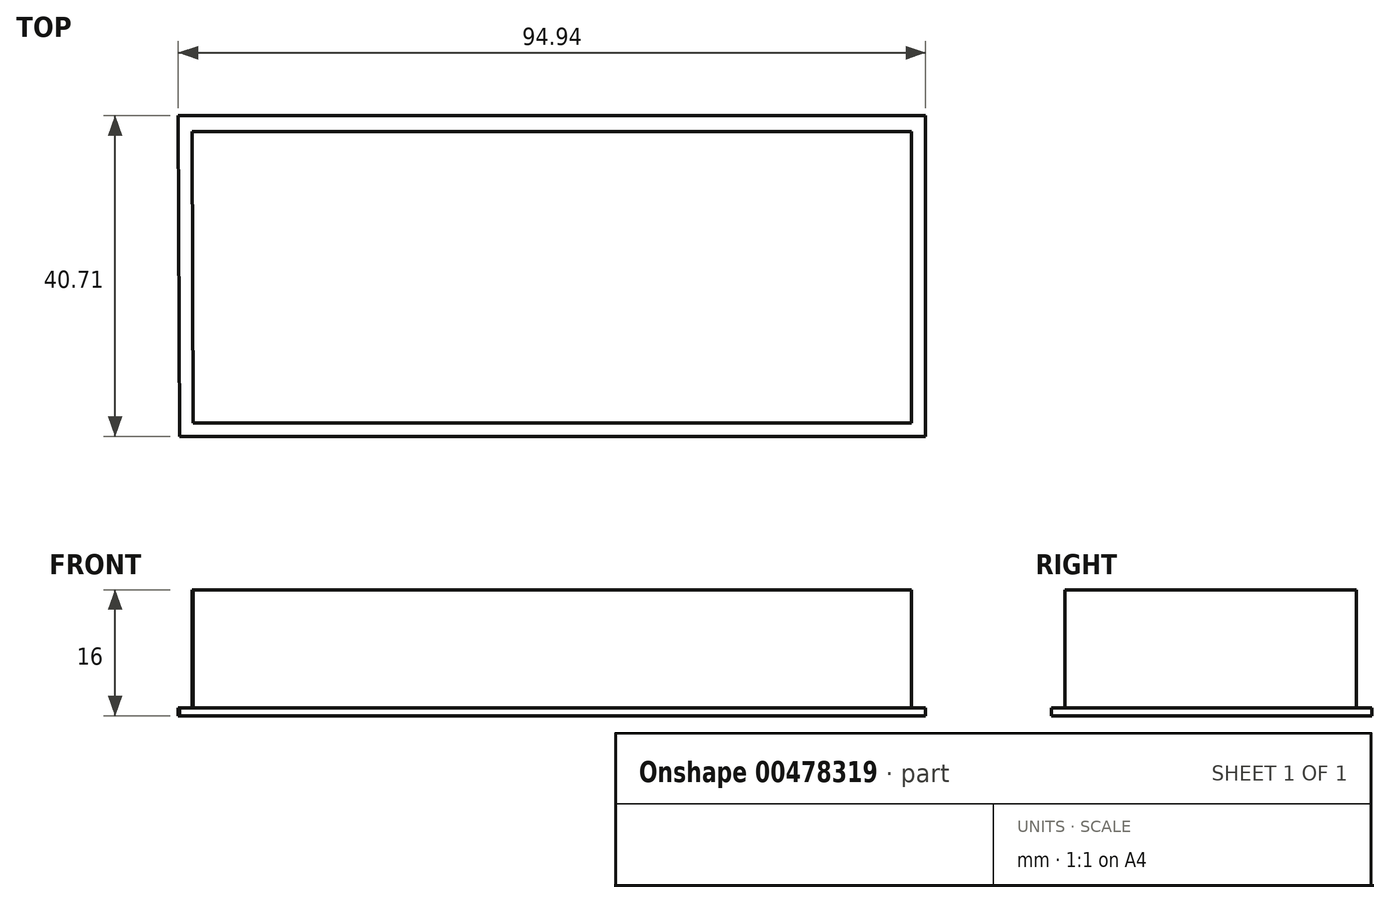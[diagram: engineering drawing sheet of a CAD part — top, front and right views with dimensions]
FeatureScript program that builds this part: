
annotation { "Feature Type Name" : "Feature", "Feature Type Description" : "" }
export const myFeature = defineFeature(function(context is Context, id is Id, definition is map)
    precondition{}
    {
        {
            var Q0;
            Q0=qCreatedBy(makeId("Top.planeOp"),FACE);
            var sketch = newSketch(context, id + "F0", { "sketchPlane" : qUnion([Q0])});
            skLineSegment(sketch, "E0", {"start": v(-48.08, 21.76) * mm, "end": v(46.86, 21.76) * mm});
            skLineSegment(sketch, "E1", {"start": v(46.86, 21.76) * mm, "end": v(46.86, -18.95) * mm});
            skLineSegment(sketch, "E2", {"start": v(46.86, -18.95) * mm, "end": v(-47.92, -18.95) * mm});
            skLineSegment(sketch, "E3", {"start": v(-47.92, -18.95) * mm, "end": v(-48.08, 21.76) * mm});
            skLineSegment(sketch, "E4", {"start": v(-46.16, -17.24) * mm, "end": v(-46.3, 19.76) * mm});
            skLineSegment(sketch, "E5", {"start": v(-46.3, 19.76) * mm, "end": v(45.04, 19.76) * mm});
            skLineSegment(sketch, "E6", {"start": v(45.04, 19.76) * mm, "end": v(45.04, -17.24) * mm});
            skLineSegment(sketch, "E7", {"start": v(-46.16, -17.24) * mm, "end": v(45.04, -17.24) * mm});
            skSolve(sketch);
        }
        {
            var Q0;
            Q0=makeQuery(id+"F0.imprint","IMPRINT",FACE,{"disambiguationData":[TD([[makeQuery(id+"F0.imprint","IMPRINT",EDGE,{"derivedFrom":sQuery(id+"F0.wireOp",EDGE,"E4")}),-1.0]])]});
            extrude(context, id + "F1", {"entities" : qUnion([Q0]), "depth" : 16 * mm});
        }
        {
            var Q0;
            Q0 = qSketchRegion(id + "F0", true);
            extrude(context, id + "F2", {"entities" : qUnion([Q0]), "operationType" : NewBodyOperationType.ADD, "depth" : 1 * mm});
        }
    });
